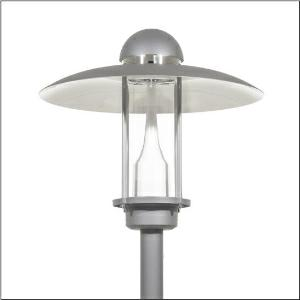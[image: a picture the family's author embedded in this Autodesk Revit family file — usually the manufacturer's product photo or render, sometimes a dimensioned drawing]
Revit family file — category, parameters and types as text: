
# Revit family: city-light_elegance_iq___st1_2a_5xa5265ef14h_e69b
name_source: partatom
category: Lighting Fixtures
units: mm (PartAtom-declared; Revit-internal decimal feet)

## family parameters
Cut with Voids When Loaded = No
Host = Face
Light Source = No
Part Type = Normal
Room Calculation Point = No
Round Connector Dimension = Use Diameter
Shared = No

## types (1)
- --- (1 x LED, 1470 lm, 10.5 W, 3000K)
    Apparent Load = 11 VA
    CIE Flux Codes = 22 62 94 98 100
    Color Rendering = 70
    Color Temperature = 3000K
    Default Elevation = 1800 mm
    Description = City-Light Elegance iQ, mast luminaire, Module 540 iQ-SR, primary light control with 3 zone facetted reflector, of plastic, silver coated, highly specular, structured, primary optical cover: cover, of PMMA, transparent, light distribution: ST1.2a, light emission: direct distribution, primary light characteristic: asymmetric, installation type: post-top, LED, High Power LED, rated luminous flux: 1.470lm, luminous efficacy: 140lm/W, light colour: 730, colour temperature: 3000K, control gear: ECG iQ, control: Auto-Match, Temp-Guard, Lumen-Switch, Night-Set, Smart-Wire, Light-Fading, Desk-Remote (wireless, voltage-free reading and setting of iQ features in the workshop via application-optimized NFC function/RFID function), optimised constant luminous flux control (CLO 2.0), Street-Remote, pre-setting: logarithmic dimming characteristic, with terminal, 6-pole, max. 2.5mm², mains connection: 230..240V, AC, 50/60Hz, start of lifetime: 11W, end of service life: 11W, reduction: 5W, luminaire housing, upper part, of aluminium, coated, Siteco® metallic grey (DB 702S), diameter: 750mm, height: 675mm, spigot size: d x l = 76 x 70mm (post-top) | with reducer (optional accessory) 60 x 70mm, post-top mast mounting element, of diecast aluminium, coated, Siteco® metallic grey (DB 702S), Module 540 iQ-SR, traffic white (RAL 9016), equipment: standard, protection rating (complete): IP65, insulation class (complete): insulation class II (safety insulation), certification: CE, ENEC, VDE, packaging unit: 1 piece

Light Distribution: ST1.2a
    Height = 675 mm
    Lamp = 1 x LED
    Lamp Light Flux = 1470 lm
    Lamp Power = 10.5 W
    Lamp count = 1
    Length = 750 mm
    Luminous efficacy = 140 lm/W
    Manufacturer = Siteco
    ModVariant = No
    Model = 5XA5265EF14H
    Number of Poles = 1
    OnlyDefault = Yes
    Power Factor = 1
    Product Name = City-Light Elegance iQ | ST1.2a
    Product group = mast luminaire | pylon top
    ProductGroupID = 6100
    Protection Class = Protection class II
    Protection Degree = IP 65
    RLX_Detail_Level = 1
    RLX_Emergency_Light_Flux = 0 lm
    RLX_Emergency_Type = 0
    RLX_Emergency_Type_DB = No
    RlxData = <blob elided: 100077 chars, md5=7154f7e1>
    Socket = socket
    Standby Power = 0 W
    System Light Flux = 1470 lm
    System Power = 11 W
    Type Comments = factory setting: luminous flux: 100 % | dim-lin: 254 | 419 mA
    Type Image = l_1006912.jpg
    URL = http://relux.com
    VarID = @adj_130213
    Voltage = 0 V
    Weight = 0.00 kg
    Width = 0 mm  [stored 0 ft]

note: [stored X ft] marks values corroborated as IEEE doubles in the binary element streams (Revit-internal decimal feet)

## geometry (parser evidence)
native form markers: Blend x4, Sweep x10
no freeform markers — native parametric forms only
